# Revit family: Soap_Dispenser-Sloan-Optima-Prism
name_source: partatom
category: Specialty Equipment
revit_build: Autodesk Revit 2016 (Build: 20150714_1515(x64)
units: mm (PartAtom-declared; Revit-internal decimal feet)

## family parameters
Always vertical = No
Cut with Voids When Loaded = No
OmniClass Number = 23.40.20.21.34
OmniClass Title = Soap Holders, Dispensers
Part Type = Normal
Room Calculation Point = No
Round Connector Dimension = Use Radius
Shared = Yes
Work Plane-Based = Yes

## types (1)
- Prism Soap Dispenser Sloan
    Assembly Code = D2020300
    CW Connection = Yes
    CWFU = 1.5
    Default Elevation = 0"
    Description = Prism Soap Dispenser Sloan
    Finish = Cast Brass-Sloan-Chrome Plated
    Global Connection Radius = 3/16"
    HW Connection = Yes
    HWFU = 1.5
    Height = 3 7/8"
    Installation Type = Deck Mounted
    Length = 5 7/8"
    Manufacturer = SLOAN
    Material = Cast Brass-Sloan-Chrome Plated
    Model = Prism Soap Dispenser Sloan
    Operation = Sensor Activated
    Revised Date = 7/32/20
    URL = https://www.sloan.com
    Vent Connection = No
    WFU = 0
    Warranty Documentation Link = https://www.sloan.com
    Waste Connection = No
    Width = 2"

## geometry (parser evidence)
native form markers: Sweep x2
no freeform markers — native parametric forms only
